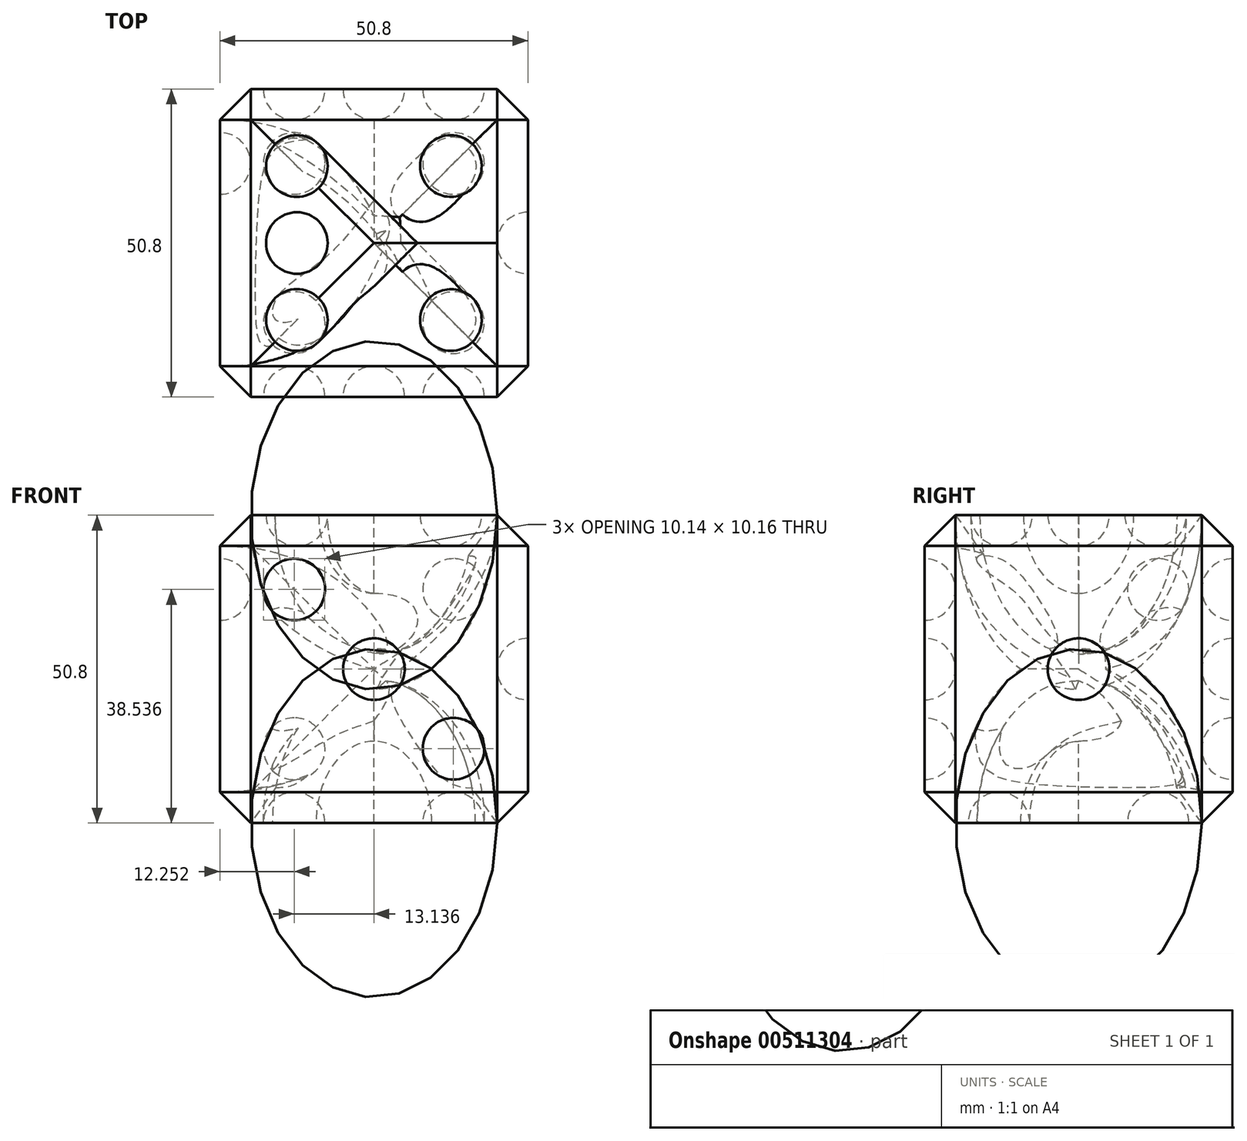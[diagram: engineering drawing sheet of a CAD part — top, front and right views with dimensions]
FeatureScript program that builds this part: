
annotation { "Feature Type Name" : "Feature", "Feature Type Description" : "" }
export const myFeature = defineFeature(function(context is Context, id is Id, definition is map)
    precondition{}
    {
        {
            var Q0;
            Q0=qCreatedBy(makeId("Top.planeOp"),FACE);
            var sketch = newSketch(context, id + "F0", { "sketchPlane" : qUnion([Q0])});
            skLineSegment(sketch, "E0.bottom", {"start": v(0, 0) * mm, "end": v(50.8, 0) * mm});
            skLineSegment(sketch, "E0.top", {"start": v(0, 50.8) * mm, "end": v(50.8, 50.8) * mm});
            skLineSegment(sketch, "E0.left", {"start": v(0, 0) * mm, "end": v(0, 50.8) * mm});
            skLineSegment(sketch, "E0.right", {"start": v(50.8, 0) * mm, "end": v(50.8, 50.8) * mm});
            skSolve(sketch);
        }
        {
            var Q0;
            Q0 = qSketchRegion(id + "F0", true);
            extrude(context, id + "F1", {"entities" : qUnion([Q0]), "depth" : 50.8 * mm, "offsetDistance" : 25.4 * mm});
        }
        {
            var Q0;
            Q0=makeQuery(id+"F1.opExtrude","CAP_EDGE",EDGE,{"disambiguationData":[OSD([sQuery(id+"F0.wireOp",EDGE,"E0.bottom")])],"isStart":false});
            var Q1;
            Q1=makeQuery(id+"F1.opExtrude","CAP_EDGE",EDGE,{"disambiguationData":[OSD([sQuery(id+"F0.wireOp",EDGE,"E0.bottom")])],"isStart":true});
            var Q2;
            Q2=makeQuery(id+"F1.opExtrude","SWEPT_EDGE",EDGE,{"disambiguationData":[OSD([sQuery(id+"F0.wireOp",EDGE,"E0.bottom"),sQuery(id+"F0.wireOp",EDGE,"E0.right")])]});
            var Q3;
            Q3=makeQuery(id+"F1.opExtrude","SWEPT_EDGE",EDGE,{"disambiguationData":[OSD([sQuery(id+"F0.wireOp",EDGE,"E0.top"),sQuery(id+"F0.wireOp",EDGE,"E0.left")])]});
            var Q4;
            Q4=makeQuery(id+"F1.opExtrude","CAP_EDGE",EDGE,{"disambiguationData":[OSD([sQuery(id+"F0.wireOp",EDGE,"E0.left")])],"isStart":false});
            var Q5;
            Q5=makeQuery(id+"F1.opExtrude","CAP_EDGE",EDGE,{"disambiguationData":[OSD([sQuery(id+"F0.wireOp",EDGE,"E0.left")])],"isStart":true});
            var Q6;
            Q6=makeQuery(id+"F1.opExtrude","SWEPT_EDGE",EDGE,{"disambiguationData":[OSD([sQuery(id+"F0.wireOp",EDGE,"E0.bottom"),sQuery(id+"F0.wireOp",EDGE,"E0.left")])]});
            var Q7;
            Q7=makeQuery(id+"F1.opExtrude","SWEPT_EDGE",EDGE,{"disambiguationData":[OSD([sQuery(id+"F0.wireOp",EDGE,"E0.top"),sQuery(id+"F0.wireOp",EDGE,"E0.right")])]});
            var Q8;
            Q8=makeQuery(id+"F1.opExtrude","CAP_EDGE",EDGE,{"disambiguationData":[OSD([sQuery(id+"F0.wireOp",EDGE,"E0.right")])],"isStart":false});
            var Q9;
            Q9=makeQuery(id+"F1.opExtrude","SWEPT_FACE",FACE,{"disambiguationData":[OSD([sQuery(id+"F0.wireOp",EDGE,"E0.right")])]});
            var Q10;
            Q10=makeQuery(id+"F1.opExtrude","CAP_EDGE",EDGE,{"disambiguationData":[OSD([sQuery(id+"F0.wireOp",EDGE,"E0.top")])],"isStart":false});
            var Q11;
            Q11=makeQuery(id+"F1.opExtrude","CAP_EDGE",EDGE,{"disambiguationData":[OSD([sQuery(id+"F0.wireOp",EDGE,"E0.top")])],"isStart":true});
            chamfer(context, id + "F2", {"entities" : qUnion([Q0, Q1, Q2, Q3, Q4, Q5, Q6, Q7, Q8, Q9, Q10, Q11]), "width" : 5.08 * mm, "tangentPropagation" : true});
        }
        {
            var Q0;
            Q0=makeQuery(id+"F1.opExtrude","SWEPT_FACE",FACE,{"disambiguationData":[OSD([sQuery(id+"F0.wireOp",EDGE,"E0.right")])]});
            var sketch = newSketch(context, id + "F3", { "sketchPlane" : qUnion([Q0])});
            skLineSegment(sketch, "E1", {"start": v(5.08, 45.72) * mm, "end": v(45.72, 5.08) * mm});
            skCircle(sketch, "E2", {"center": v(25.4, 25.4) * mm, "radius": 5.08 * mm});
            skSolve(sketch);
        }
        {
            var Q0;
            {var subQ0=sQuery(id+"F3.wireOp",EDGE,"E2");var subQ1=sQuery(id+"F3.wireOp",EDGE,"E1");var subQ2=makeQuery(id+"F3.imprint","INTERSECT",VERTEX,{"disambiguationData":[OD(0.0)],"derivedFrom":[subQ1,subQ0]});Q0=makeQuery(id+"F3.imprint","IMPRINT",FACE,{"disambiguationData":[TD([[makeQuery(id+"F3.imprint","IMPRINT",EDGE,{"disambiguationData":[TD([[subQ2,-1.0]])],"derivedFrom":subQ1}),1.0]])]});}
            var Q1;
            Q1=sQuery(id+"F3.wireOp",EDGE,"E1");
            revolve(context, id + "F4", {"operationType" : NewBodyOperationType.REMOVE, "entities" : qUnion([Q0]), "axis" : qUnion([Q1]), "revolveType" : RevolveType.FULL, "oppositeDirection" : true});
        }
        {
            var Q0;
            Q0=makeQuery(id+"F1.opExtrude","SWEPT_FACE",FACE,{"disambiguationData":[OSD([sQuery(id+"F0.wireOp",EDGE,"E0.left")])]});
            var sketch = newSketch(context, id + "F5", { "sketchPlane" : qUnion([Q0])});
            skLineSegment(sketch, "E3", {"start": v(-45.72, 45.72) * mm, "end": v(-5.08, 5.08) * mm});
            skCircle(sketch, "E4", {"center": v(-38.54, 38.54) * mm, "radius": 5.08 * mm});
            skCircle(sketch, "E5", {"center": v(-12.26, 12.26) * mm, "radius": 5.08 * mm});
            skSolve(sketch);
        }
        {
            var Q0;
            {var subQ0=sQuery(id+"F5.wireOp",EDGE,"E4");var subQ1=sQuery(id+"F5.wireOp",EDGE,"E3");var subQ2=makeQuery(id+"F5.imprint","INTERSECT",VERTEX,{"disambiguationData":[OD(0.0)],"derivedFrom":[subQ1,subQ0]});Q0=makeQuery(id+"F5.imprint","IMPRINT",FACE,{"disambiguationData":[TD([[makeQuery(id+"F5.imprint","IMPRINT",EDGE,{"disambiguationData":[TD([[subQ2,-1.0]])],"derivedFrom":subQ1}),1.0]])]});}
            var Q1;
            {var subQ0=sQuery(id+"F5.wireOp",EDGE,"E5");var subQ1=sQuery(id+"F5.wireOp",EDGE,"E3");var subQ2=makeQuery(id+"F5.imprint","INTERSECT",VERTEX,{"disambiguationData":[OD(0.0)],"derivedFrom":[subQ1,subQ0]});Q1=makeQuery(id+"F5.imprint","IMPRINT",FACE,{"disambiguationData":[TD([[makeQuery(id+"F5.imprint","IMPRINT",EDGE,{"disambiguationData":[TD([[subQ2,-1.0]])],"derivedFrom":subQ1}),1.0]])]});}
            var Q2;
            Q2=sQuery(id+"F5.wireOp",EDGE,"E3");
            revolve(context, id + "F6", {"operationType" : NewBodyOperationType.REMOVE, "entities" : qUnion([Q0, Q1]), "axis" : qUnion([Q2]), "revolveType" : RevolveType.FULL});
        }
        {
            var Q0;
            Q0=makeQuery(id+"F1.opExtrude","CAP_FACE",FACE,{"disambiguationData":[OSD([sQuery(id+"F0.wireOp",EDGE,"E0.bottom"),sQuery(id+"F0.wireOp",EDGE,"E0.top"),sQuery(id+"F0.wireOp",EDGE,"E0.left"),sQuery(id+"F0.wireOp",EDGE,"E0.right")])],"isStart":true});
            var sketch = newSketch(context, id + "F7", { "sketchPlane" : qUnion([Q0])});
            skLineSegment(sketch, "E6", {"start": v(5.08, -45.72) * mm, "end": v(45.72, -5.08) * mm});
            skLineSegment(sketch, "E7", {"start": v(45.72, -45.72) * mm, "end": v(5.08, -5.08) * mm});
            skCircle(sketch, "E8", {"center": v(12.26, -38.54) * mm, "radius": 5.08 * mm});
            skCircle(sketch, "E9", {"center": v(12.26, -12.26) * mm, "radius": 5.08 * mm});
            skCircle(sketch, "E10", {"center": v(38.54, -12.26) * mm, "radius": 5.08 * mm});
            skCircle(sketch, "E11", {"center": v(38.54, -38.54) * mm, "radius": 5.08 * mm});
            skSolve(sketch);
        }
        {
            var Q0;
            {var subQ0=sQuery(id+"F7.wireOp",EDGE,"E9");var subQ1=sQuery(id+"F7.wireOp",EDGE,"E7");var subQ2=makeQuery(id+"F7.imprint","INTERSECT",VERTEX,{"disambiguationData":[OD(0.0)],"derivedFrom":[subQ1,subQ0]});Q0=makeQuery(id+"F7.imprint","IMPRINT",FACE,{"disambiguationData":[TD([[makeQuery(id+"F7.imprint","IMPRINT",EDGE,{"disambiguationData":[TD([[subQ2,-1.0]])],"derivedFrom":subQ1}),-1.0]])]});}
            var Q1;
            {var subQ0=sQuery(id+"F7.wireOp",EDGE,"E11");var subQ1=sQuery(id+"F7.wireOp",EDGE,"E7");var subQ2=makeQuery(id+"F7.imprint","INTERSECT",VERTEX,{"disambiguationData":[OD(0.0)],"derivedFrom":[subQ1,subQ0]});Q1=makeQuery(id+"F7.imprint","IMPRINT",FACE,{"disambiguationData":[TD([[makeQuery(id+"F7.imprint","IMPRINT",EDGE,{"disambiguationData":[TD([[subQ2,-1.0]])],"derivedFrom":subQ1}),-1.0]])]});}
            var Q2;
            Q2=sQuery(id+"F7.wireOp",EDGE,"E7");
            revolve(context, id + "F8", {"operationType" : NewBodyOperationType.REMOVE, "entities" : qUnion([Q0, Q1]), "axis" : qUnion([Q2]), "revolveType" : RevolveType.FULL, "oppositeDirection" : true});
        }
        {
            var Q0;
            {var subQ0=sQuery(id+"F7.wireOp",EDGE,"E8");var subQ1=sQuery(id+"F7.wireOp",EDGE,"E6");var subQ2=makeQuery(id+"F7.imprint","INTERSECT",VERTEX,{"disambiguationData":[OD(0.0)],"derivedFrom":[subQ1,subQ0]});Q0=makeQuery(id+"F7.imprint","IMPRINT",FACE,{"disambiguationData":[TD([[makeQuery(id+"F7.imprint","IMPRINT",EDGE,{"disambiguationData":[TD([[subQ2,-1.0]])],"derivedFrom":subQ1}),1.0]])]});}
            var Q1;
            {var subQ0=sQuery(id+"F7.wireOp",EDGE,"E10");var subQ1=sQuery(id+"F7.wireOp",EDGE,"E6");var subQ2=makeQuery(id+"F7.imprint","INTERSECT",VERTEX,{"disambiguationData":[OD(0.0)],"derivedFrom":[subQ1,subQ0]});Q1=makeQuery(id+"F7.imprint","IMPRINT",FACE,{"disambiguationData":[TD([[makeQuery(id+"F7.imprint","IMPRINT",EDGE,{"disambiguationData":[TD([[subQ2,-1.0]])],"derivedFrom":subQ1}),1.0]])]});}
            var Q2;
            Q2=sQuery(id+"F7.wireOp",EDGE,"E6");
            revolve(context, id + "F9", {"operationType" : NewBodyOperationType.REMOVE, "entities" : qUnion([Q0, Q1]), "axis" : qUnion([Q2]), "revolveType" : RevolveType.FULL, "oppositeDirection" : true});
        }
        {
            var Q0;
            Q0=makeQuery(id+"F1.opExtrude","SWEPT_FACE",FACE,{"disambiguationData":[OSD([sQuery(id+"F0.wireOp",EDGE,"E0.top")])]});
            var sketch = newSketch(context, id + "F10", { "sketchPlane" : qUnion([Q0])});
            skLineSegment(sketch, "E12", {"start": v(-45.72, 45.72) * mm, "end": v(-5.08, 5.08) * mm});
            skLineSegment(sketch, "E13", {"start": v(-45.72, 5.08) * mm, "end": v(-5.08, 45.72) * mm});
            skCircle(sketch, "E14", {"center": v(-25.4, 25.4) * mm, "radius": 5.08 * mm});
            skCircle(sketch, "E15", {"center": v(-38.54, 38.54) * mm, "radius": 5.08 * mm});
            skCircle(sketch, "E16", {"center": v(-12.26, 38.54) * mm, "radius": 5.08 * mm});
            skCircle(sketch, "E17", {"center": v(-12.26, 12.26) * mm, "radius": 5.08 * mm});
            skCircle(sketch, "E18", {"center": v(-38.54, 12.26) * mm, "radius": 5.08 * mm});
            skSolve(sketch);
        }
        {
            var Q0;
            {var subQ0=sQuery(id+"F10.wireOp",EDGE,"E15");var subQ1=sQuery(id+"F10.wireOp",EDGE,"E12");var subQ2=makeQuery(id+"F10.imprint","INTERSECT",VERTEX,{"disambiguationData":[OD(0.0)],"derivedFrom":[subQ1,subQ0]});Q0=makeQuery(id+"F10.imprint","IMPRINT",FACE,{"disambiguationData":[TD([[makeQuery(id+"F10.imprint","IMPRINT",EDGE,{"disambiguationData":[TD([[subQ2,-1.0]])],"derivedFrom":subQ1}),1.0]])]});}
            var Q1;
            {var subQ0=sQuery(id+"F10.wireOp",EDGE,"E17");var subQ1=sQuery(id+"F10.wireOp",EDGE,"E12");var subQ2=makeQuery(id+"F10.imprint","INTERSECT",VERTEX,{"disambiguationData":[OD(0.0)],"derivedFrom":[subQ1,subQ0]});Q1=makeQuery(id+"F10.imprint","IMPRINT",FACE,{"disambiguationData":[TD([[makeQuery(id+"F10.imprint","IMPRINT",EDGE,{"disambiguationData":[TD([[subQ2,-1.0]])],"derivedFrom":subQ1}),-1.0]])]});}
            var Q2;
            Q2=sQuery(id+"F10.wireOp",EDGE,"E12");
            revolve(context, id + "F11", {"operationType" : NewBodyOperationType.REMOVE, "entities" : qUnion([Q0, Q1]), "axis" : qUnion([Q2]), "revolveType" : RevolveType.FULL});
        }
        {
            var Q0;
            {var subQ0=sQuery(id+"F10.wireOp",EDGE,"E18");var subQ1=sQuery(id+"F10.wireOp",EDGE,"E13");var subQ2=makeQuery(id+"F10.imprint","INTERSECT",VERTEX,{"disambiguationData":[OD(0.0)],"derivedFrom":[subQ1,subQ0]});Q0=makeQuery(id+"F10.imprint","IMPRINT",FACE,{"disambiguationData":[TD([[makeQuery(id+"F10.imprint","IMPRINT",EDGE,{"disambiguationData":[TD([[subQ2,-1.0]])],"derivedFrom":subQ1}),-1.0]])]});}
            var Q1;
            {var subQ0=sQuery(id+"F10.wireOp",EDGE,"E13");var subQ1=sQuery(id+"F10.wireOp",EDGE,"E12");var subQ2=makeQuery(id+"F10.imprint","INTERSECT",VERTEX,{"derivedFrom":[subQ1,subQ0]});Q1=makeQuery(id+"F10.imprint","IMPRINT",FACE,{"disambiguationData":[TD([[makeQuery(id+"F10.imprint","IMPRINT",EDGE,{"disambiguationData":[TD([[subQ2,-1.0]])],"derivedFrom":subQ1}),-1.0]])]});}
            var Q2;
            {var subQ0=sQuery(id+"F10.wireOp",EDGE,"E13");var subQ1=sQuery(id+"F10.wireOp",EDGE,"E12");var subQ2=makeQuery(id+"F10.imprint","INTERSECT",VERTEX,{"derivedFrom":[subQ1,subQ0]});Q2=makeQuery(id+"F10.imprint","IMPRINT",FACE,{"disambiguationData":[TD([[makeQuery(id+"F10.imprint","IMPRINT",EDGE,{"disambiguationData":[TD([[subQ2,-1.0]])],"derivedFrom":subQ1}),1.0]])]});}
            var Q3;
            {var subQ0=sQuery(id+"F10.wireOp",EDGE,"E16");var subQ1=sQuery(id+"F10.wireOp",EDGE,"E13");var subQ2=makeQuery(id+"F10.imprint","INTERSECT",VERTEX,{"disambiguationData":[OD(0.0)],"derivedFrom":[subQ1,subQ0]});Q3=makeQuery(id+"F10.imprint","IMPRINT",FACE,{"disambiguationData":[TD([[makeQuery(id+"F10.imprint","IMPRINT",EDGE,{"disambiguationData":[TD([[subQ2,-1.0]])],"derivedFrom":subQ1}),-1.0]])]});}
            var Q4;
            Q4=sQuery(id+"F10.wireOp",EDGE,"E13");
            revolve(context, id + "F12", {"operationType" : NewBodyOperationType.REMOVE, "entities" : qUnion([Q0, Q1, Q2, Q3]), "axis" : qUnion([Q4]), "revolveType" : RevolveType.FULL, "oppositeDirection" : true});
        }
        {
            var Q0;
            Q0=makeQuery(id+"F1.opExtrude","SWEPT_FACE",FACE,{"disambiguationData":[OSD([sQuery(id+"F0.wireOp",EDGE,"E0.bottom")])]});
            var sketch = newSketch(context, id + "F13", { "sketchPlane" : qUnion([Q0])});
            skLineSegment(sketch, "E19", {"start": v(5.08, 45.72) * mm, "end": v(45.72, 5.08) * mm});
            skCircle(sketch, "E20", {"center": v(25.4, 25.4) * mm, "radius": 5.08 * mm});
            skCircle(sketch, "E21", {"center": v(38.54, 12.26) * mm, "radius": 5.08 * mm});
            skCircle(sketch, "E22", {"center": v(12.26, 38.54) * mm, "radius": 5.08 * mm});
            skSolve(sketch);
        }
        {
            var Q0;
            {var subQ0=sQuery(id+"F13.wireOp",EDGE,"E22");var subQ1=sQuery(id+"F13.wireOp",EDGE,"E19");var subQ2=makeQuery(id+"F13.imprint","INTERSECT",VERTEX,{"disambiguationData":[OD(0.0)],"derivedFrom":[subQ1,subQ0]});Q0=makeQuery(id+"F13.imprint","IMPRINT",FACE,{"disambiguationData":[TD([[makeQuery(id+"F13.imprint","IMPRINT",EDGE,{"disambiguationData":[TD([[subQ2,-1.0]])],"derivedFrom":subQ1}),1.0]])]});}
            var Q1;
            {var subQ0=sQuery(id+"F13.wireOp",EDGE,"E20");var subQ1=sQuery(id+"F13.wireOp",EDGE,"E19");var subQ2=makeQuery(id+"F13.imprint","INTERSECT",VERTEX,{"disambiguationData":[OD(0.0)],"derivedFrom":[subQ1,subQ0]});Q1=makeQuery(id+"F13.imprint","IMPRINT",FACE,{"disambiguationData":[TD([[makeQuery(id+"F13.imprint","IMPRINT",EDGE,{"disambiguationData":[TD([[subQ2,-1.0]])],"derivedFrom":subQ1}),1.0]])]});}
            var Q2;
            {var subQ0=sQuery(id+"F13.wireOp",EDGE,"E21");var subQ1=sQuery(id+"F13.wireOp",EDGE,"E19");var subQ2=makeQuery(id+"F13.imprint","INTERSECT",VERTEX,{"disambiguationData":[OD(0.0)],"derivedFrom":[subQ1,subQ0]});Q2=makeQuery(id+"F13.imprint","IMPRINT",FACE,{"disambiguationData":[TD([[makeQuery(id+"F13.imprint","IMPRINT",EDGE,{"disambiguationData":[TD([[subQ2,-1.0]])],"derivedFrom":subQ1}),1.0]])]});}
            var Q3;
            Q3=sQuery(id+"F13.wireOp",EDGE,"E19");
            revolve(context, id + "F14", {"operationType" : NewBodyOperationType.REMOVE, "entities" : qUnion([Q0, Q1, Q2]), "axis" : qUnion([Q3]), "revolveType" : RevolveType.FULL, "oppositeDirection" : true});
        }
        {
            var Q0;
            Q0=makeQuery(id+"F1.opExtrude","CAP_FACE",FACE,{"disambiguationData":[OSD([sQuery(id+"F0.wireOp",EDGE,"E0.bottom"),sQuery(id+"F0.wireOp",EDGE,"E0.top"),sQuery(id+"F0.wireOp",EDGE,"E0.left"),sQuery(id+"F0.wireOp",EDGE,"E0.right")])],"isStart":false});
            var sketch = newSketch(context, id + "F15", { "sketchPlane" : qUnion([Q0])});
            skLineSegment(sketch, "E23", {"start": v(45.72, 5.08) * mm, "end": v(5.08, 45.72) * mm});
            skLineSegment(sketch, "E24", {"start": v(45.72, 45.72) * mm, "end": v(5.08, 5.08) * mm});
            skLineSegment(sketch, "E25", {"start": v(45.72, 25.4) * mm, "end": v(5.08, 25.4) * mm});
            skCircle(sketch, "E26", {"center": v(38.1, 25.4) * mm, "radius": 5.08 * mm});
            skCircle(sketch, "E27", {"center": v(38.1, 12.7) * mm, "radius": 5.08 * mm});
            skCircle(sketch, "E28", {"center": v(38.1, 38.1) * mm, "radius": 5.08 * mm});
            skCircle(sketch, "E29", {"center": v(12.7, 38.1) * mm, "radius": 5.08 * mm});
            skCircle(sketch, "E30", {"center": v(12.7, 25.4) * mm, "radius": 5.08 * mm});
            skCircle(sketch, "E31", {"center": v(12.7, 12.7) * mm, "radius": 5.08 * mm});
            skSolve(sketch);
        }
        {
            var Q0;
            {var subQ0=sQuery(id+"F15.wireOp",EDGE,"E29");var subQ1=sQuery(id+"F15.wireOp",EDGE,"E23");var subQ2=makeQuery(id+"F15.imprint","INTERSECT",VERTEX,{"disambiguationData":[OD(0.0)],"derivedFrom":[subQ1,subQ0]});Q0=makeQuery(id+"F15.imprint","IMPRINT",FACE,{"disambiguationData":[TD([[makeQuery(id+"F15.imprint","IMPRINT",EDGE,{"disambiguationData":[TD([[subQ2,-1.0]])],"derivedFrom":subQ1}),1.0]])]});}
            var Q1;
            {var subQ0=sQuery(id+"F15.wireOp",EDGE,"E27");var subQ1=sQuery(id+"F15.wireOp",EDGE,"E23");var subQ2=makeQuery(id+"F15.imprint","INTERSECT",VERTEX,{"disambiguationData":[OD(0.0)],"derivedFrom":[subQ1,subQ0]});Q1=makeQuery(id+"F15.imprint","IMPRINT",FACE,{"disambiguationData":[TD([[makeQuery(id+"F15.imprint","IMPRINT",EDGE,{"disambiguationData":[TD([[subQ2,-1.0]])],"derivedFrom":subQ1}),1.0]])]});}
            var Q2;
            Q2=sQuery(id+"F15.wireOp",EDGE,"E23");
            revolve(context, id + "F16", {"operationType" : NewBodyOperationType.REMOVE, "entities" : qUnion([Q0, Q1]), "axis" : qUnion([Q2]), "revolveType" : RevolveType.FULL});
        }
        {
            var Q0;
            {var subQ0=sQuery(id+"F15.wireOp",EDGE,"E30");var subQ1=sQuery(id+"F15.wireOp",EDGE,"E25");var subQ2=makeQuery(id+"F15.imprint","INTERSECT",VERTEX,{"disambiguationData":[OD(0.0)],"derivedFrom":[subQ1,subQ0]});Q0=makeQuery(id+"F15.imprint","IMPRINT",FACE,{"disambiguationData":[TD([[makeQuery(id+"F15.imprint","IMPRINT",EDGE,{"disambiguationData":[TD([[subQ2,-1.0]])],"derivedFrom":subQ1}),1.0]])]});}
            var Q1;
            {var subQ0=sQuery(id+"F15.wireOp",EDGE,"E26");var subQ1=sQuery(id+"F15.wireOp",EDGE,"E25");var subQ2=makeQuery(id+"F15.imprint","INTERSECT",VERTEX,{"disambiguationData":[OD(0.0)],"derivedFrom":[subQ1,subQ0]});Q1=makeQuery(id+"F15.imprint","IMPRINT",FACE,{"disambiguationData":[TD([[makeQuery(id+"F15.imprint","IMPRINT",EDGE,{"disambiguationData":[TD([[subQ2,-1.0]])],"derivedFrom":subQ1}),1.0]])]});}
            var Q2;
            Q2=sQuery(id+"F15.wireOp",EDGE,"E25");
            revolve(context, id + "F17", {"operationType" : NewBodyOperationType.REMOVE, "entities" : qUnion([Q0, Q1]), "axis" : qUnion([Q2]), "revolveType" : RevolveType.FULL, "oppositeDirection" : true});
        }
        {
            var Q0;
            {var subQ0=sQuery(id+"F15.wireOp",EDGE,"E31");var subQ1=sQuery(id+"F15.wireOp",EDGE,"E24");var subQ2=makeQuery(id+"F15.imprint","INTERSECT",VERTEX,{"disambiguationData":[OD(0.0)],"derivedFrom":[subQ1,subQ0]});Q0=makeQuery(id+"F15.imprint","IMPRINT",FACE,{"disambiguationData":[TD([[makeQuery(id+"F15.imprint","IMPRINT",EDGE,{"disambiguationData":[TD([[subQ2,-1.0]])],"derivedFrom":subQ1}),1.0]])]});}
            var Q1;
            {var subQ0=sQuery(id+"F15.wireOp",EDGE,"E28");var subQ1=sQuery(id+"F15.wireOp",EDGE,"E24");var subQ2=makeQuery(id+"F15.imprint","INTERSECT",VERTEX,{"disambiguationData":[OD(0.0)],"derivedFrom":[subQ1,subQ0]});Q1=makeQuery(id+"F15.imprint","IMPRINT",FACE,{"disambiguationData":[TD([[makeQuery(id+"F15.imprint","IMPRINT",EDGE,{"disambiguationData":[TD([[subQ2,-1.0]])],"derivedFrom":subQ1}),-1.0]])]});}
            var Q2;
            Q2=sQuery(id+"F15.wireOp",EDGE,"E24");
            revolve(context, id + "F18", {"operationType" : NewBodyOperationType.REMOVE, "entities" : qUnion([Q0, Q1]), "axis" : qUnion([Q2]), "revolveType" : RevolveType.FULL});
        }
    });
